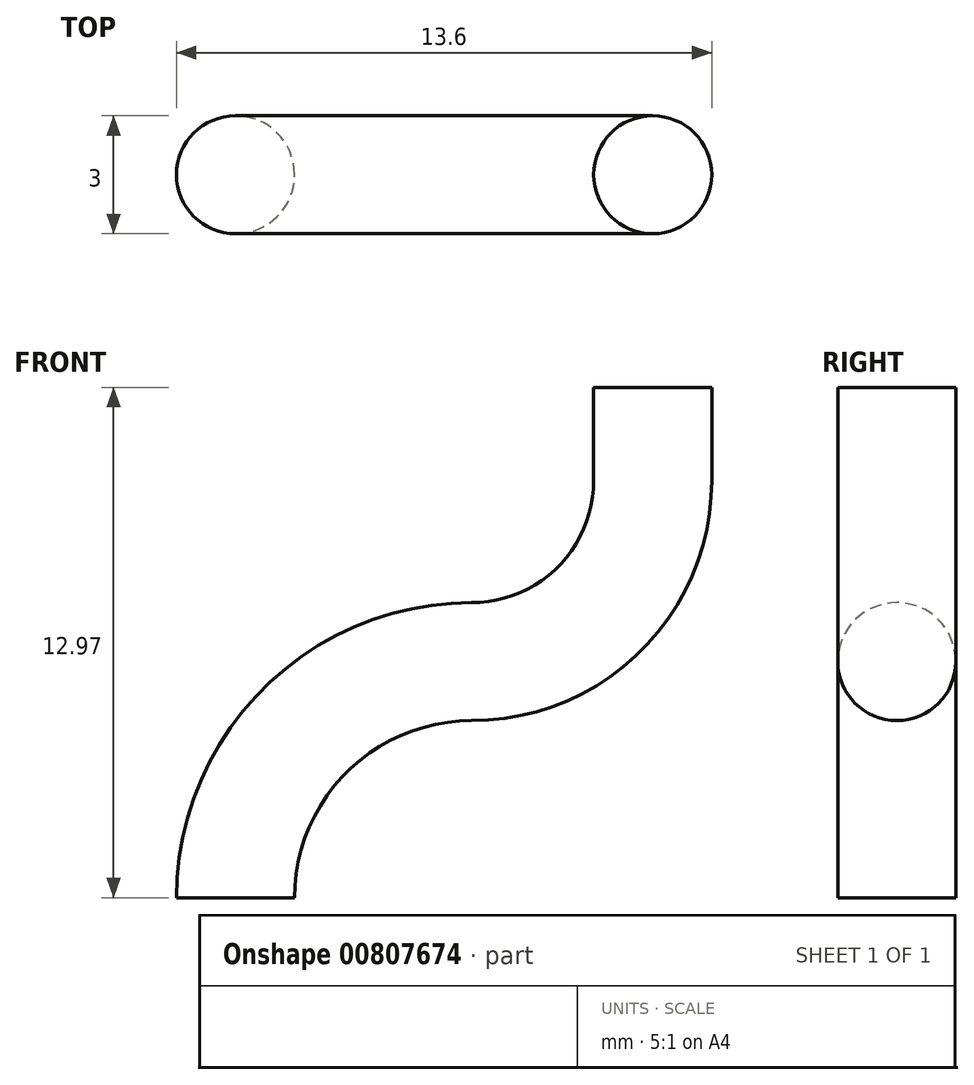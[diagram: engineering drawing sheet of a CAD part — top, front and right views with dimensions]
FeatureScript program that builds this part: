
annotation { "Feature Type Name" : "Feature", "Feature Type Description" : "" }
export const myFeature = defineFeature(function(context is Context, id is Id, definition is map)
    precondition{}
    {
        {
            var Q0;
            Q0=qCreatedBy(makeId("Front.planeOp"),FACE);
            var sketch = newSketch(context, id + "F0", { "sketchPlane" : qUnion([Q0])});
            skArc(sketch, "E0", {"start": v(0, 6) * mm, "mid": v(-4.24, 4.24) * mm, "end": v(-6, 0) * mm});
            skArc(sketch, "E1", {"start": v(0, 6) * mm, "mid": v(3.25, 7.35) * mm, "end": v(4.6, 10.6) * mm});
            skLineSegment(sketch, "E2", {"start": v(4.6, 10.6) * mm, "end": v(4.6, 12.97) * mm});
            skSolve(sketch);
        }
        {
            var Q0;
            Q0=qCreatedBy(makeId("Top.planeOp"),FACE);
            var sketch = newSketch(context, id + "F1", { "sketchPlane" : qUnion([Q0])});
            skCircle(sketch, "E3", {"center": v(-6, 0) * mm, "radius": 1.5 * mm});
            skSolve(sketch);
        }
        {
            var Q0;
            Q0=makeQuery(id+"F1.imprint","IMPRINT",FACE,{"disambiguationData":[TD([[makeQuery(id+"F1.imprint","IMPRINT",EDGE,{"derivedFrom":sQuery(id+"F1.wireOp",EDGE,"E3")}),1.0]])]});
            var Q1;
            Q1=sQuery(id+"F0.wireOp",EDGE,"E0");
            var Q2;
            Q2=sQuery(id+"F0.wireOp",EDGE,"E1");
            var Q3;
            Q3=sQuery(id+"F0.wireOp",EDGE,"E2");
            sweep(context, id + "F2", {"profiles" : qUnion([Q0]), "path" : qUnion([Q1, Q2, Q3])});
        }
    });
